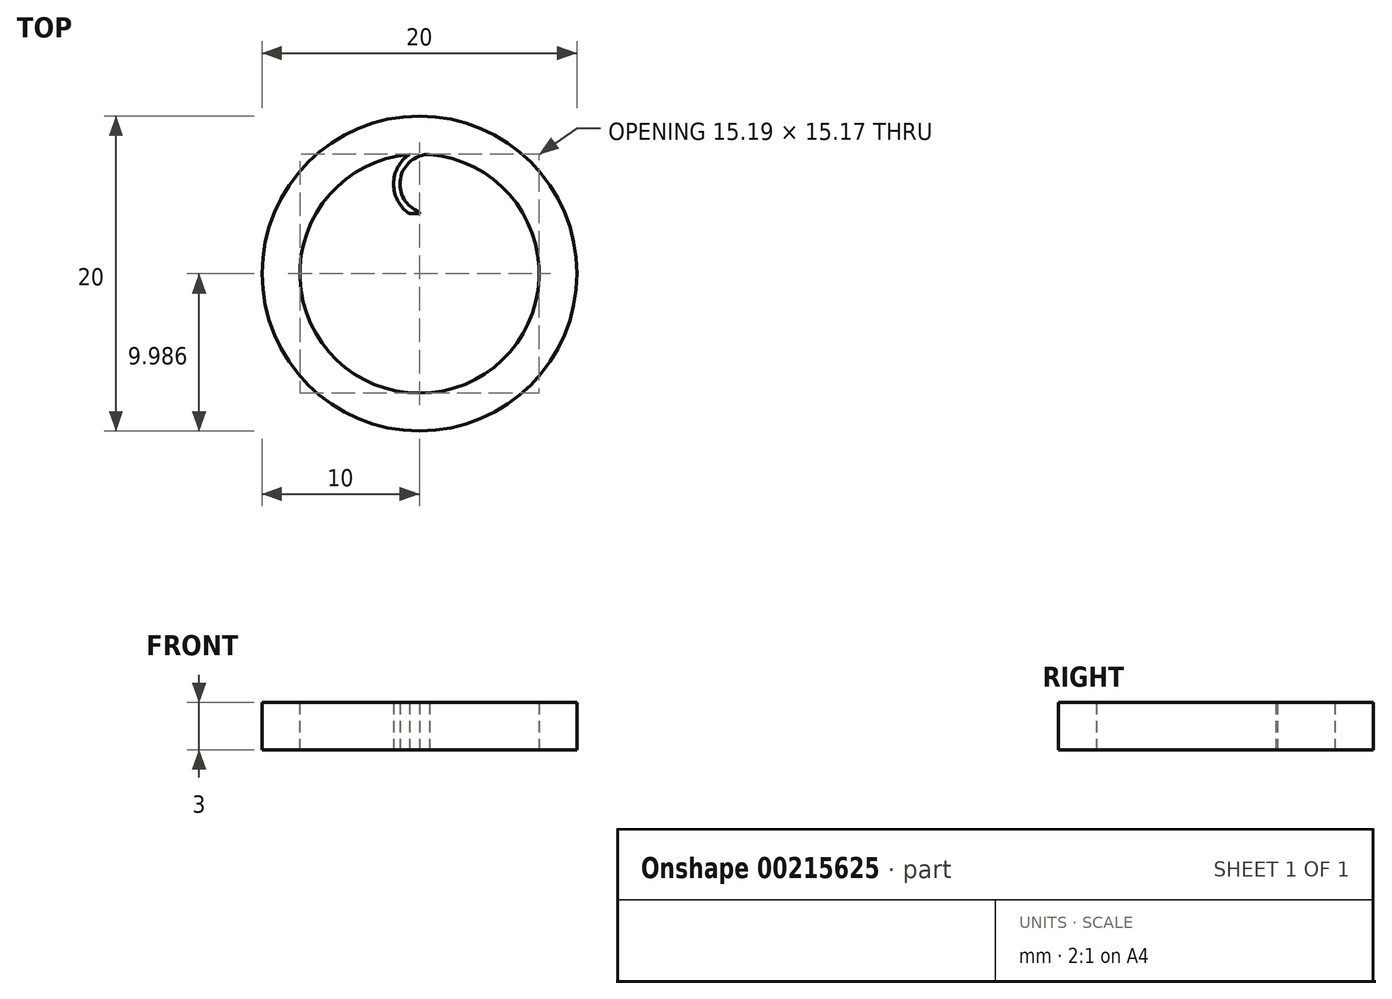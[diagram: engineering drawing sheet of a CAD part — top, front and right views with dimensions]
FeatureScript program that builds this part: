
annotation { "Feature Type Name" : "Feature", "Feature Type Description" : "" }
export const myFeature = defineFeature(function(context is Context, id is Id, definition is map)
    precondition{}
    {
        {
            var Q0;
            Q0=qCreatedBy(makeId("Top.planeOp"),FACE);
            var sketch = newSketch(context, id + "F0", { "sketchPlane" : qUnion([Q0])});
            skCircle(sketch, "E0", {"center": v(0, 0) * mm, "radius": 7.6 * mm});
            skCircle(sketch, "E1", {"center": v(0, 0) * mm, "radius": 10 * mm});
            skSolve(sketch);
        }
        {
            var Q0;
            Q0 = qSketchRegion(id + "F0", true);
            extrude(context, id + "F1", {"entities" : qUnion([Q0]), "depth" : 3 * mm});
        }
        {
            var Q0;
            Q0=qCreatedBy(makeId("Top.planeOp"),FACE);
            var sketch = newSketch(context, id + "F2", { "sketchPlane" : qUnion([Q0])});
            skCircle(sketch, "E2.0", {"center": v(0, 0) * mm, "radius": 7.6 * mm});
            skLineSegment(sketch, "E3", {"start": v(-0.65, 3.8) * mm, "end": v(0.65, 3.8) * mm});
            skLineSegment(sketch, "E4", {"start": v(0.65, 3.8) * mm, "end": v(0.65, 7.57) * mm, "construction": true});
            skLineSegment(sketch, "E5", {"start": v(0, 0) * mm, "end": v(0, 3.8) * mm, "construction": true});
            skArc(sketch, "E6", {"start": v(0.65, 7.57) * mm, "mid": v(-1.24, 5.69) * mm, "end": v(0.65, 3.8) * mm});
            skArc(sketch, "E7", {"start": v(0.65, 7.97) * mm, "mid": v(-1.64, 5.69) * mm, "end": v(0.65, 3.4) * mm});
            skLineSegment(sketch, "E8", {"start": v(0, 3.8) * mm, "end": v(0, 3.91) * mm});
            skSolve(sketch);
        }
        {
            var Q0;
            {var subQ0=sQuery(id+"F2.wireOp",EDGE,"N0US4zlP-Tiaw-jmlp-6OOO-6123ut0QMheT");Q0=makeQuery(id+"F2.imprint","IMPRINT",FACE,{"disambiguationData":[TD([[makeQuery(id+"F2.imprint","IMPRINT",EDGE,{"derivedFrom":subQ0}),1.0]])]});}
            var Q1;
            {var subQ7=sQuery(id+"F2.wireOp",EDGE,"E8");Q1=makeQuery(id+"F2.imprint","IMPRINT",FACE,{"disambiguationData":[TD([[makeQuery(id+"F2.imprint","IMPRINT",EDGE,{"derivedFrom":subQ7}),1.0]])]});}
            var Q2;
            Q2=makeQuery(id+"F1.opExtrude","CAP_FACE",FACE,{"disambiguationData":[OSD([sQuery(id+"F0.wireOp",EDGE,"E0"),sQuery(id+"F0.wireOp",EDGE,"E1")])],"isStart":false});
            extrude(context, id + "F3", {"entities" : qUnion([Q0, Q1]), "operationType" : NewBodyOperationType.ADD, "endBound" : BoundingType.UP_TO_SURFACE, "endBoundEntityFace" : qUnion([Q2]), "depth" : 5 * mm});
        }
    });
